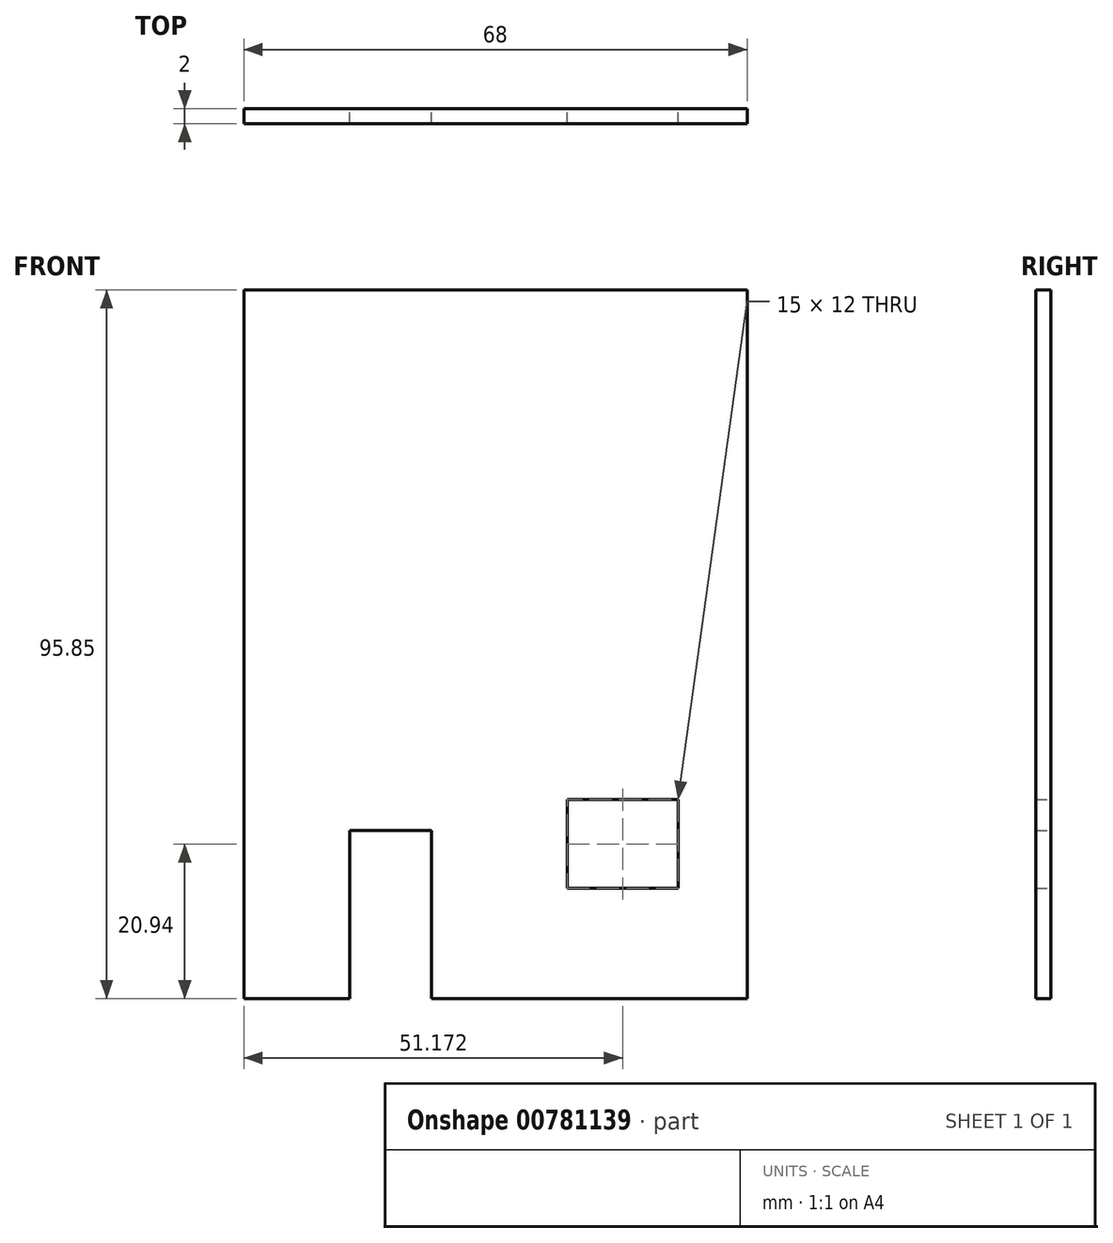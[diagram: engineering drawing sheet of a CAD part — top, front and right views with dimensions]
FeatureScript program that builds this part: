
annotation { "Feature Type Name" : "Feature", "Feature Type Description" : "" }
export const myFeature = defineFeature(function(context is Context, id is Id, definition is map)
    precondition{}
    {
        {
            var Q0;
            Q0=qCreatedBy(makeId("Front.planeOp"),FACE);
            var sketch = newSketch(context, id + "F0", { "sketchPlane" : qUnion([Q0])});
            skLineSegment(sketch, "E0.bottom", {"start": v(-24.33, 39.3) * mm, "end": v(43.67, 39.3) * mm});
            skLineSegment(sketch, "E0.top", {"start": v(-24.33, -56.56) * mm, "end": v(43.67, -56.56) * mm});
            skLineSegment(sketch, "E0.left", {"start": v(-24.33, 39.3) * mm, "end": v(-24.33, -56.56) * mm});
            skLineSegment(sketch, "E0.right", {"start": v(43.67, 39.3) * mm, "end": v(43.67, -56.56) * mm});
            skSolve(sketch);
        }
        {
            var Q0;
            Q0=makeQuery(id+"F0.imprint","IMPRINT",FACE,{"disambiguationData":[TD([[makeQuery(id+"F0.imprint","IMPRINT",EDGE,{"derivedFrom":sQuery(id+"F0.wireOp",EDGE,"E0.bottom")}),-1.0]])]});
            var sketch = newSketch(context, id + "F1", { "sketchPlane" : qUnion([Q0])});
            skLineSegment(sketch, "E1.bottom", {"start": v(-10.02, -33.82) * mm, "end": v(0.98, -33.82) * mm});
            skLineSegment(sketch, "E1.top", {"start": v(-10.02, -56.82) * mm, "end": v(0.98, -56.82) * mm});
            skLineSegment(sketch, "E1.left", {"start": v(-10.02, -33.82) * mm, "end": v(-10.02, -56.82) * mm});
            skLineSegment(sketch, "E1.right", {"start": v(0.98, -33.82) * mm, "end": v(0.98, -56.82) * mm});
            skLineSegment(sketch, "E2.bottom", {"start": v(19.34, -29.62) * mm, "end": v(34.34, -29.62) * mm});
            skLineSegment(sketch, "E2.top", {"start": v(19.34, -41.62) * mm, "end": v(34.34, -41.62) * mm});
            skLineSegment(sketch, "E2.left", {"start": v(19.34, -29.62) * mm, "end": v(19.34, -41.62) * mm});
            skLineSegment(sketch, "E2.right", {"start": v(34.34, -29.62) * mm, "end": v(34.34, -41.62) * mm});
            skSolve(sketch);
        }
        {
            var Q0;
            {var subQ2=sQuery(id+"F1.wireOp",EDGE,"E1.bottom");Q0=makeQuery(id+"F1.imprint","IMPRINT",FACE,{"disambiguationData":[TD([[makeQuery(id+"F1.imprint","IMPRINT",EDGE,{"derivedFrom":subQ2}),1.0]])]});}
            extrude(context, id + "F2", {"entities" : qUnion([Q0]), "depth" : 2 * mm, "offsetDistance" : 25 * mm});
        }
    });
